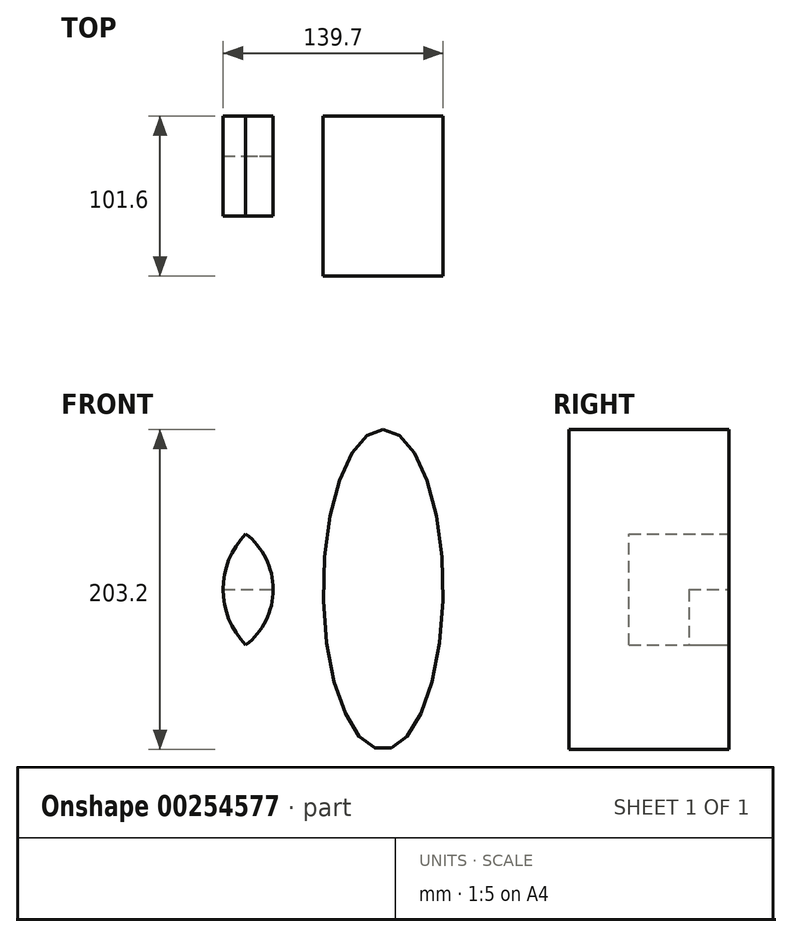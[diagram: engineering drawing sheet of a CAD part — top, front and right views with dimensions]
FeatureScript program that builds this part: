
annotation { "Feature Type Name" : "Feature", "Feature Type Description" : "" }
export const myFeature = defineFeature(function(context is Context, id is Id, definition is map)
    precondition{}
    {
        {
            var Q0;
            Q0=qCreatedBy(makeId("Front.planeOp"),FACE);
            var sketch = newSketch(context, id + "F0", { "sketchPlane" : qUnion([Q0])});
            skCircle(sketch, "E0", {"center": v(-76.2, 0) * mm, "radius": 44.45 * mm});
            skLineSegment(sketch, "E1", {"start": v(-76.2, 0) * mm, "end": v(0, 0) * mm});
            skCircle(sketch, "E2", {"center": v(-12.7, 0) * mm, "radius": 50.8 * mm});
            skLineSegment(sketch, "E3", {"start": v(-63.5, 0) * mm, "end": v(-31.75, 0) * mm});
            skEllipse(sketch, "E4", {"center": v(38.1, 0) * mm, "majorRadius": 101.6 * mm, "minorRadius": 38.1 * mm, "majorAxis": v(0, 1)});
            skLineSegment(sketch, "E5", {"start": v(38.1, 0) * mm, "end": v(38.1, 101.6) * mm});
            skSolve(sketch);
        }
        {
            var Q0;
            {var subQ0=sQuery(id+"F0.wireOp",EDGE,"E2");var subQ1=sQuery(id+"F0.wireOp",EDGE,"E0");var subQ2=makeQuery(id+"F0.imprint","INTERSECT",VERTEX,{"disambiguationData":[OD(0.0)],"derivedFrom":[subQ1,subQ0]});Q0=makeQuery(id+"F0.imprint","IMPRINT",FACE,{"disambiguationData":[TD([[makeQuery(id+"F0.imprint","IMPRINT",EDGE,{"disambiguationData":[TD([[subQ2,-1.0]])],"derivedFrom":subQ1}),1.0]])]});}
            extrude(context, id + "F1", {"entities" : qUnion([Q0]), "depth" : 25.4 * mm});
        }
        {
            var Q0;
            {var subQ1=sQuery(id+"F0.wireOp",EDGE,"E0");var subQ3=sQuery(id+"F0.wireOp",EDGE,"E2");var subQ4=makeQuery(id+"F0.imprint","INTERSECT",VERTEX,{"disambiguationData":[OD(0.0)],"derivedFrom":[subQ1,subQ3]});Q0=makeQuery(id+"F0.imprint","IMPRINT",FACE,{"disambiguationData":[TD([[makeQuery(id+"F0.imprint","IMPRINT",EDGE,{"disambiguationData":[TD([[subQ4,1.0]])],"derivedFrom":subQ3}),1.0]])]});}
            var Q1;
            {var subQ0=sQuery(id+"F0.wireOp",EDGE,"E3");Q1=makeQuery(id+"F0.imprint","IMPRINT",FACE,{"disambiguationData":[TD([[makeQuery(id+"F0.imprint","IMPRINT",EDGE,{"derivedFrom":subQ0}),1.0]])]});}
            var Q2;
            {var subQ0=sQuery(id+"F0.wireOp",EDGE,"E3");Q2=makeQuery(id+"F0.imprint","IMPRINT",FACE,{"disambiguationData":[TD([[makeQuery(id+"F0.imprint","IMPRINT",EDGE,{"derivedFrom":subQ0}),-1.0]])]});}
            var Q3;
            {var subQ1=sQuery(id+"F0.wireOp",EDGE,"E0");var subQ3=sQuery(id+"F0.wireOp",EDGE,"E2");var subQ4=makeQuery(id+"F0.imprint","INTERSECT",VERTEX,{"disambiguationData":[OD(1.0)],"derivedFrom":[subQ1,subQ3]});Q3=makeQuery(id+"F0.imprint","IMPRINT",FACE,{"disambiguationData":[TD([[makeQuery(id+"F0.imprint","IMPRINT",EDGE,{"disambiguationData":[TD([[subQ4,-1.0]])],"derivedFrom":subQ3}),1.0]])]});}
            extrude(context, id + "F2", {"entities" : qUnion([Q0, Q1, Q2, Q3]), "depth" : 63.5 * mm});
        }
        {
            var Q0;
            {var subQ0=sQuery(id+"F0.wireOp",EDGE,"E5");Q0=makeQuery(id+"F0.imprint","IMPRINT",FACE,{"disambiguationData":[TD([[makeQuery(id+"F0.imprint","IMPRINT",EDGE,{"derivedFrom":subQ0}),1.0]])]});}
            var Q1;
            {var subQ0=sQuery(id+"F0.wireOp",EDGE,"E5");Q1=makeQuery(id+"F0.imprint","IMPRINT",FACE,{"disambiguationData":[TD([[makeQuery(id+"F0.imprint","IMPRINT",EDGE,{"derivedFrom":subQ0}),-1.0]])]});}
            var Q2;
            {var subQ0=sQuery(id+"F0.wireOp",EDGE,"E2");var subQ1=makeQuery(id+"F0.imprint","INTERSECT",VERTEX,{"derivedFrom":[subQ0,sQuery(id+"F0.wireOp",EDGE,"E5")]});Q2=makeQuery(id+"F0.imprint","IMPRINT",FACE,{"disambiguationData":[TD([[makeQuery(id+"F0.imprint","IMPRINT",EDGE,{"disambiguationData":[TD([[subQ1,-1.0]])],"derivedFrom":subQ0}),1.0]])]});}
            extrude(context, id + "F3", {"entities" : qUnion([Q0, Q1, Q2]), "depth" : 101.6 * mm});
        }
    });
